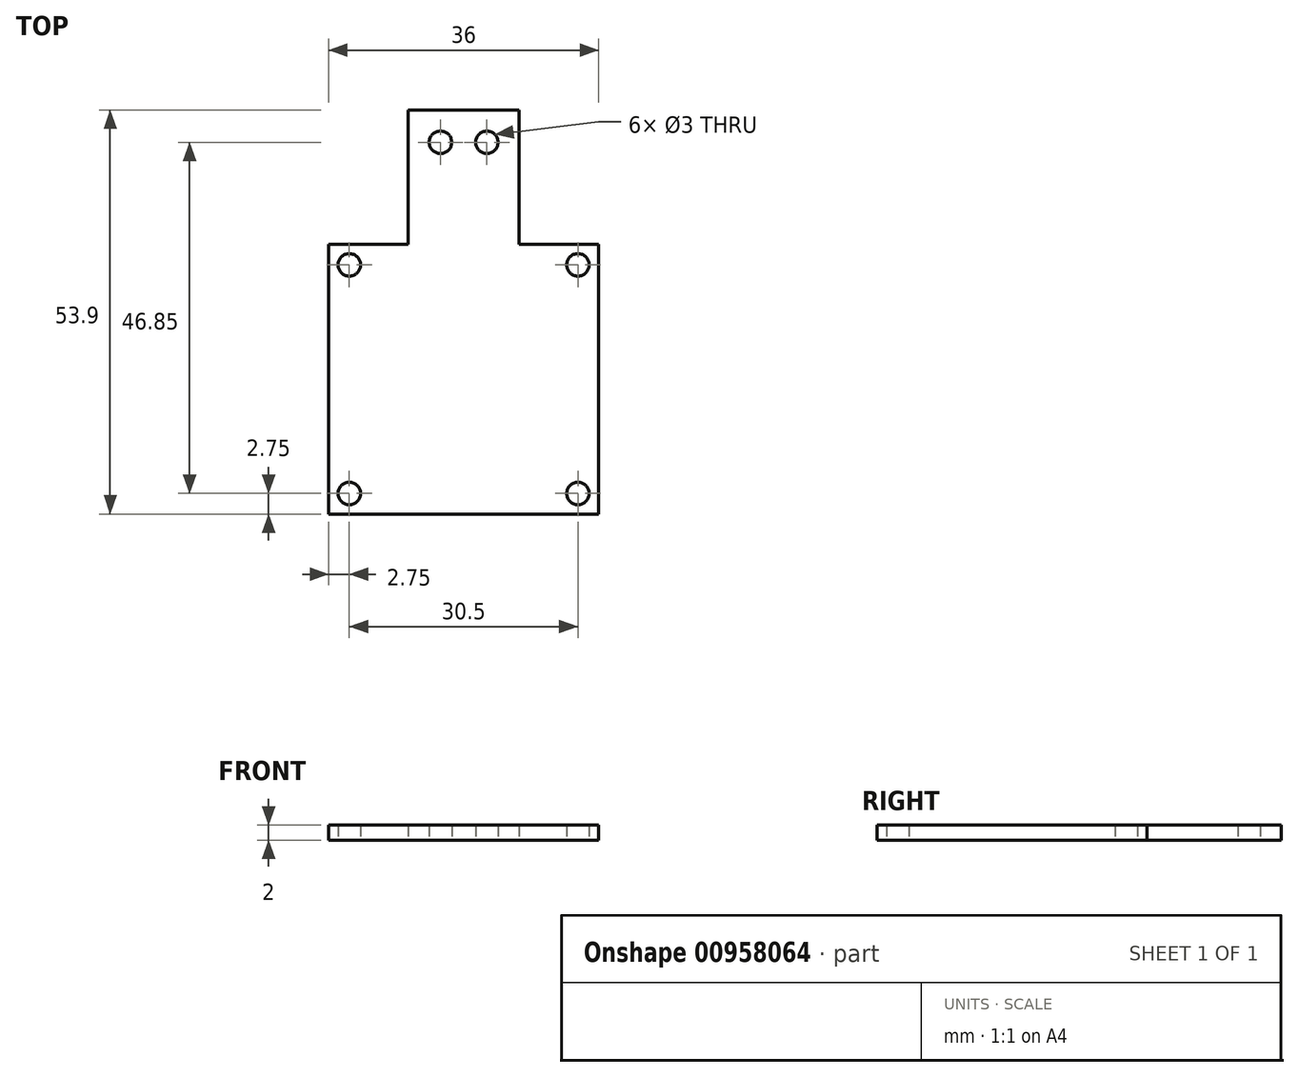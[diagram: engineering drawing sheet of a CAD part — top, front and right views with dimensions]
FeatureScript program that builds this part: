
annotation { "Feature Type Name" : "Feature", "Feature Type Description" : "" }
export const myFeature = defineFeature(function(context is Context, id is Id, definition is map)
    precondition{}
    {
        {
            var Q0;
            Q0=qCreatedBy(makeId("Top.planeOp"),FACE);
            var sketch = newSketch(context, id + "F0", { "sketchPlane" : qUnion([Q0])});
            skLineSegment(sketch, "E0", {"start": v(-18, 18) * mm, "end": v(-18, -18) * mm});
            skLineSegment(sketch, "E1", {"start": v(18, -18) * mm, "end": v(18, 18) * mm});
            skLineSegment(sketch, "E2", {"start": v(18, 18) * mm, "end": v(-18, 18) * mm});
            skLineSegment(sketch, "E3", {"start": v(-18, -18) * mm, "end": v(18, -18) * mm});
            skLineSegment(sketch, "E4", {"start": v(-7.4, 18) * mm, "end": v(-7.4, 35.9) * mm});
            skLineSegment(sketch, "E5", {"start": v(-7.4, 35.9) * mm, "end": v(7.4, 35.9) * mm});
            skLineSegment(sketch, "E6", {"start": v(7.4, 35.9) * mm, "end": v(7.4, 18) * mm});
            skCircle(sketch, "E7", {"center": v(-15.25, 15.25) * mm, "radius": 1.5 * mm});
            skCircle(sketch, "E8", {"center": v(-15.25, -15.25) * mm, "radius": 1.5 * mm});
            skCircle(sketch, "E9.MirrorC", {"center": v(15.25, -15.25) * mm, "radius": 1.5 * mm});
            skCircle(sketch, "E10.MirrorC", {"center": v(15.25, 15.25) * mm, "radius": 1.5 * mm});
            skCircle(sketch, "E11", {"center": v(-3.09, 31.6) * mm, "radius": 1.5 * mm});
            skCircle(sketch, "E12", {"center": v(3.1, 31.6) * mm, "radius": 1.5 * mm});
            skSolve(sketch);
        }
        {
            var Q0;
            Q0=qSketchRegion(id+"F0",true);
            extrude(context, id + "F1", {"entities" : qUnion([Q0]), "depth" : 2 * mm, "offsetDistance" : 25 * mm});
        }
    });
